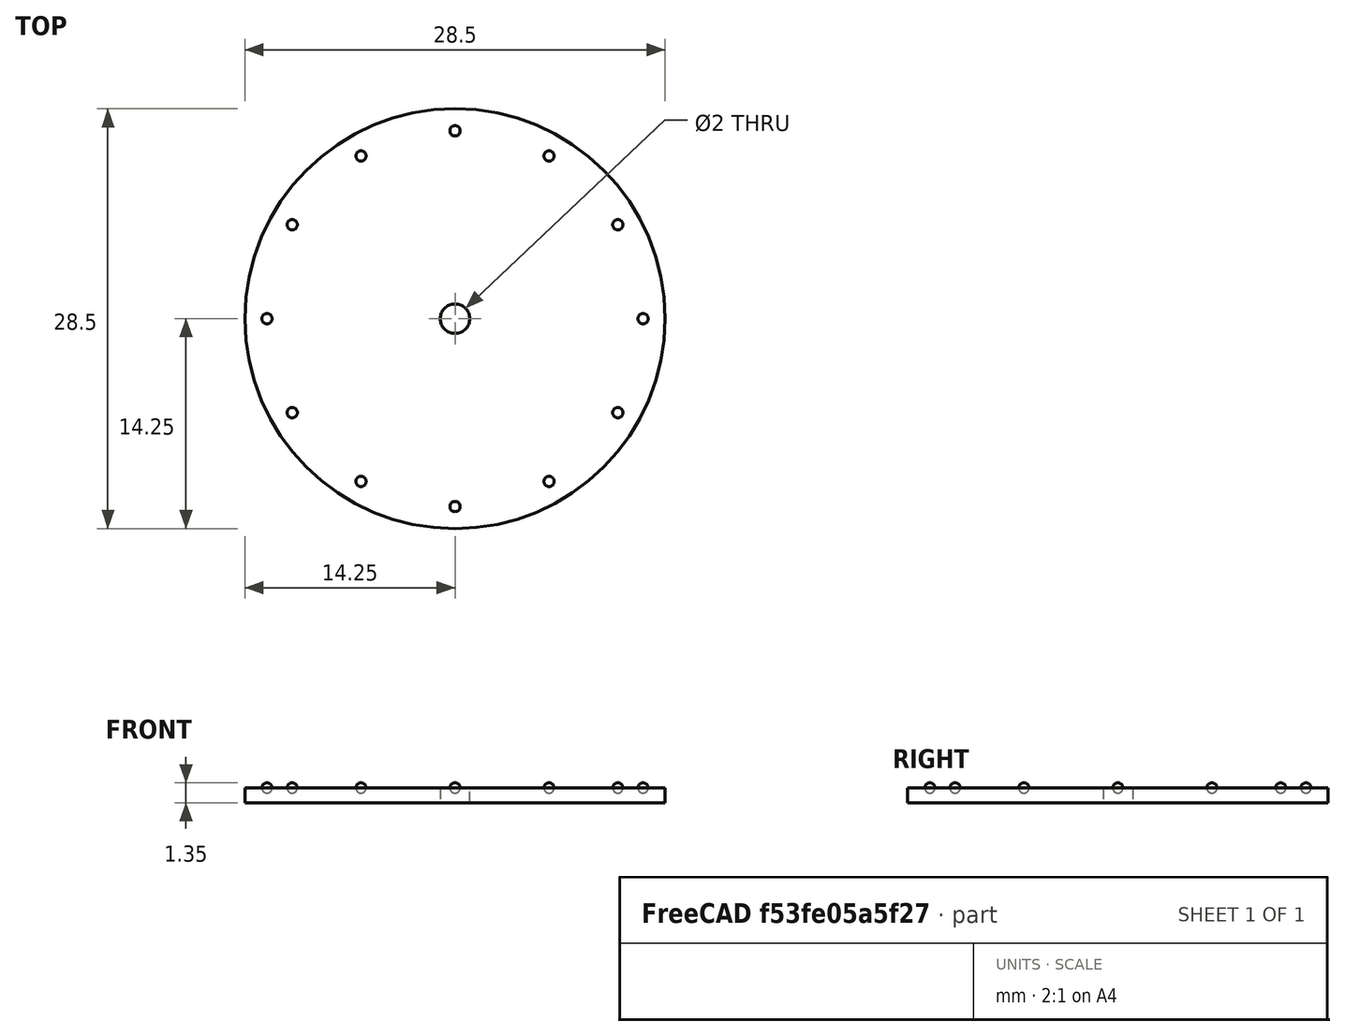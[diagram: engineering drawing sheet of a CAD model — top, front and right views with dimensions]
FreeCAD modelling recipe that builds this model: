
FCSTD DOCUMENT  (FreeCAD 0.19R20415 (Git))
Label: Vostok_Amphibia_dial
License: All rights reserved
LicenseURL: http://en.wikipedia.org/wiki/All_rights_reserved
objects: Part::Sphere×2, Part::FeaturePython×2, Sketcher::SketchObject×1, PartDesign::Pad×1, PartDesign::Body×1
note: 8 computed .brp shape members not serialized (recipe doc carries the construction recipe); baked Part::Feature solids carry a one-line shape summary decoded from their .brp

FEATURE [Sketcher::SketchObject] Sketch029
  MapMode = 5
  Support = -> [XY_Plane006]
  sketch-geometry (2):
    g0: Circle CenterX=0 CenterY=0 CenterZ=0 NormalX=0 NormalY=0 NormalZ=1 AngleXU=0 Radius=14.25
    g1: Circle CenterX=0 CenterY=0 CenterZ=0 NormalX=0 NormalY=0 NormalZ=1 AngleXU=0 Radius=1
  constraints (4):
    c: Coincident(g0,g-1)
    c: Diameter(g0) = 28.5
    c: Coincident(g1,g0)
    c: Diameter(g1) = 2
FEATURE [PartDesign::Pad] Pad005
  AllowMultiFace = false
  Length = 1
  Length2 = 100
  Profile = -> Sketch029
  Type = 0
FEATURE [PartDesign::Body] Body006  label="Dial"
  Group = -> [Sketch029,Pad005]
  Origin = -> Origin006
  Tip = -> Pad005
FEATURE [Part::Sphere] Sphere  label="Sphère"
  Angle1 = -90
  Angle2 = 90
  Angle3 = 360
  AttacherType = Attacher::AttachEngine3D
  Placement = pos=(12.75,0,1) rot=(0,0,1;0rad)
  Radius = 0.35
FEATURE [Part::FeaturePython] Array  # Draft array (typed FeaturePython)
  Angle = 360
  ArrayType = 1
  Axis = (0,0,1)
  Base = -> Sphere
  Center = (0,0,0)
  Fuse = true
  IntervalAxis = (0,0,0)
  IntervalX = (1,0,0)
  IntervalY = (0,1,0)
  IntervalZ = (0,0,1)
  NumberCircles = 2
  NumberPolar = 12
  NumberX = 1
  NumberY = 1
  NumberZ = 1
  RadialDistance = 1
  Symmetry = 1
  TangentialDistance = 1
FEATURE [Part::Sphere] Sphere001  label="Sphère001"
  Angle1 = -90
  Angle2 = 90
  Angle3 = 360
  AttacherType = Attacher::AttachEngine3D
  Placement = pos=(12.75,0,1) rot=(0,0,1;0rad)
  Radius = 0.35
FEATURE [Part::FeaturePython] Array001  # Draft array (typed FeaturePython)
  Angle = 300
  ArrayType = 1
  Axis = (0,0,1)
  Base = -> Sphere001
  Center = (0,0,0)
  Fuse = true
  IntervalAxis = (0,0,0)
  IntervalX = (1,0,0)
  IntervalY = (0,1,0)
  IntervalZ = (0,0,1)
  NumberCircles = 2
  NumberPolar = 11
  NumberX = 1
  NumberY = 1
  NumberZ = 1
  RadialDistance = 1
  Symmetry = 1
  TangentialDistance = 1
